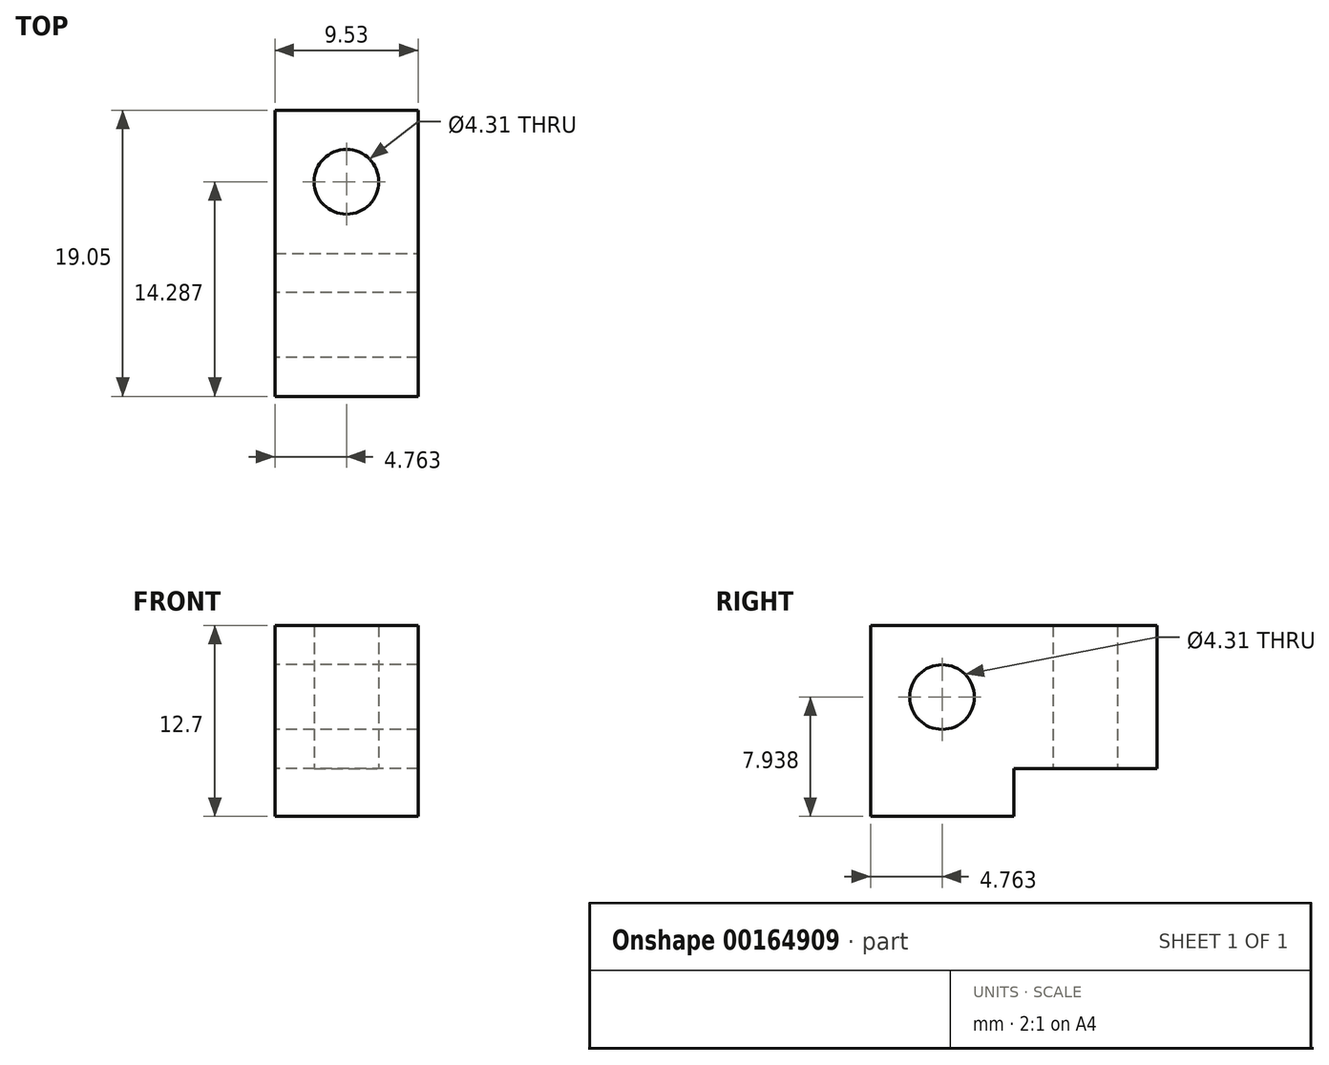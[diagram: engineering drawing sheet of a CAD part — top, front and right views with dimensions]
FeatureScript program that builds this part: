
annotation { "Feature Type Name" : "Feature", "Feature Type Description" : "" }
export const myFeature = defineFeature(function(context is Context, id is Id, definition is map)
    precondition{}
    {
        {
            var Q0;
            Q0=qCreatedBy(makeId("Top.planeOp"),FACE);
            var sketch = newSketch(context, id + "F0", { "sketchPlane" : qUnion([Q0])});
            skLineSegment(sketch, "E0.bottom", {"start": v(0, 0) * mm, "end": v(9.53, 0) * mm});
            skLineSegment(sketch, "E0.top", {"start": v(0, 19.05) * mm, "end": v(9.52, 19.05) * mm});
            skLineSegment(sketch, "E0.left", {"start": v(0, 0) * mm, "end": v(0, 19.05) * mm});
            skLineSegment(sketch, "E0.right", {"start": v(9.53, 0) * mm, "end": v(9.52, 19.05) * mm});
            skLineSegment(sketch, "E1", {"start": v(4.76, 19.05) * mm, "end": v(4.76, 14.29) * mm, "construction": true});
            skLineSegment(sketch, "E2", {"start": v(4.76, 14.29) * mm, "end": v(9.53, 14.29) * mm, "construction": true});
            skCircle(sketch, "E3", {"center": v(4.76, 14.29) * mm, "radius": 2.15 * mm});
            skSolve(sketch);
        }
        {
            var Q0;
            Q0=qSketchRegion(id+"F0",true);
            extrude(context, id + "F1", {"entities" : qUnion([Q0]), "depth" : 15.88 * mm});
        }
        {
            var Q0;
            Q0=makeQuery(id+"F1.opExtrude","SWEPT_FACE",FACE,{"disambiguationData":[OSD([sQuery(id+"F0.wireOp",EDGE,"E0.top")])]});
            var sketch = newSketch(context, id + "F2", { "sketchPlane" : qUnion([Q0])});
            skLineSegment(sketch, "E4.bottom", {"start": v(-9.52, 0) * mm, "end": v(0, 0) * mm});
            skLineSegment(sketch, "E4.top", {"start": v(-9.52, 3.18) * mm, "end": v(0, 3.18) * mm});
            skLineSegment(sketch, "E4.left", {"start": v(-9.52, 0) * mm, "end": v(-9.52, 3.18) * mm});
            skLineSegment(sketch, "E4.right", {"start": v(0, 0) * mm, "end": v(0, 3.18) * mm});
            skLineSegment(sketch, "E5.bottom", {"start": v(0, 15.88) * mm, "end": v(-9.53, 15.88) * mm});
            skLineSegment(sketch, "E5.top", {"start": v(0, 12.7) * mm, "end": v(-9.52, 12.7) * mm});
            skLineSegment(sketch, "E5.left", {"start": v(0, 15.88) * mm, "end": v(0, 12.7) * mm});
            skLineSegment(sketch, "E5.right", {"start": v(-9.52, 15.88) * mm, "end": v(-9.52, 12.7) * mm});
            skSolve(sketch);
        }
        {
            var Q0;
            Q0=qSketchRegion(id+"F2",true);
            extrude(context, id + "F3", {"entities" : qUnion([Q0]), "operationType" : NewBodyOperationType.REMOVE, "oppositeDirection" : true, "depth" : 9.52 * mm});
        }
        {
            var Q0;
            Q0=makeQuery(id+"F1.opExtrude","SWEPT_FACE",FACE,{"disambiguationData":[OSD([sQuery(id+"F0.wireOp",EDGE,"E0.left")])]});
            var sketch = newSketch(context, id + "F4", { "sketchPlane" : qUnion([Q0])});
            skLineSegment(sketch, "E6", {"start": v(-4.76, 0) * mm, "end": v(-4.76, 15.88) * mm, "construction": true});
            skCircle(sketch, "E7", {"center": v(-4.76, 7.94) * mm, "radius": 2.15 * mm});
            skSolve(sketch);
        }
        {
            var Q0;
            Q0=qSketchRegion(id+"F4",true);
            var Q1;
            Q1=makeQuery(id+"F1.opExtrude","SWEPT_FACE",FACE,{"disambiguationData":[OSD([sQuery(id+"F0.wireOp",EDGE,"E0.right")])]});
            extrude(context, id + "F5", {"entities" : qUnion([Q0]), "operationType" : NewBodyOperationType.REMOVE, "endBound" : BoundingType.UP_TO_SURFACE, "oppositeDirection" : true, "endBoundEntityFace" : qUnion([Q1]), "depth" : 6.35 * mm});
        }
        {
            var Q0;
            Q0=makeQuery(id+"F3.boolean.opBoolean","COPY",FACE,{"derivedFrom":makeQuery(id+"F3.opExtrude","CAP_FACE",FACE,{"disambiguationData":[OSD([sQuery(id+"F2.wireOp",EDGE,"E5.bottom"),sQuery(id+"F2.wireOp",EDGE,"E5.top"),sQuery(id+"F2.wireOp",EDGE,"E5.left"),sQuery(id+"F2.wireOp",EDGE,"E5.right")])],"isStart":false})});
            var Q1;
            Q1=makeQuery(id+"F1.opExtrude","SWEPT_FACE",FACE,{"disambiguationData":[OSD([sQuery(id+"F0.wireOp",EDGE,"E0.bottom")])]});
            extrude(context, id + "F6", {"entities" : qUnion([Q0]), "operationType" : NewBodyOperationType.REMOVE, "endBound" : BoundingType.UP_TO_SURFACE, "oppositeDirection" : true, "endBoundEntityFace" : qUnion([Q1]), "depth" : 25.4 * mm});
        }
    });
